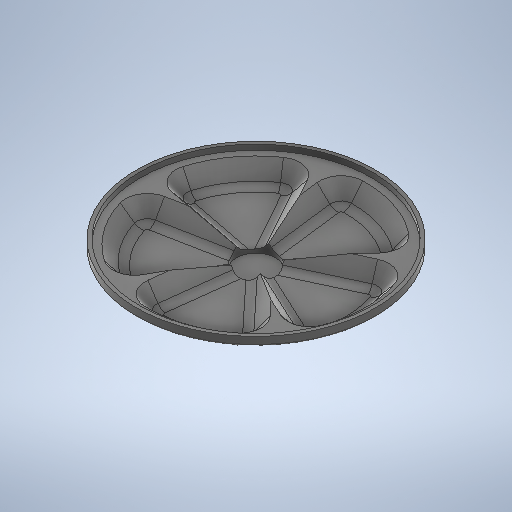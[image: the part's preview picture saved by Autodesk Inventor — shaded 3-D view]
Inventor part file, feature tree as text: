
AUTODESK INVENTOR PART (.ipt)
format: ipt  version: 2025.3 (Build 293356000, 356)  size: 781,312 bytes
history: native  units: mm
features: sketch x4, extrude x3, fillet x3, shell x1
ambient origin geometry x8: Origin, YZ Plane, XZ Plane, XY Plane, X Axis, Y Axis, Z Axis, Center Point
bodies: Body1 (feature_tree)
feature tree (11):
  extrude  "Extrusión2"  Depth=1100.0mm
  fillet  "Empalme2"  Radius=50.0mm
  extrude  "Extrusión3"  Depth=8.726646mm
  fillet  "Empalme3"  Radius=50.0mm
  extrude  "Extrusión4"  Depth=80.0mm
  fillet  "Empalme4"  Radius=1370.0mm
  shell  "Vaciado2"  Thickness=50.0mm
  sketch  "Boceto5"  dims[d21=50.0mm d22=8.726646mm d23=50.0mm d25=360.0deg]
  sketch  "Boceto - Patrón circular2"  dims[d18=1370.0mm d19=1100.0mm d20=50.0mm]
  sketch  "Boceto6"  dims[d27=150.0mm d28=6.981317mm d29=80.0mm d30=1370.0mm d31=50.0mm d32=0.0mm]
  sketch  "Boceto7"  dims[d33=10.0mm d34=265.0mm d35=170.0mm d36=0.0mm d37=10.0mm d38=20.0mm]
